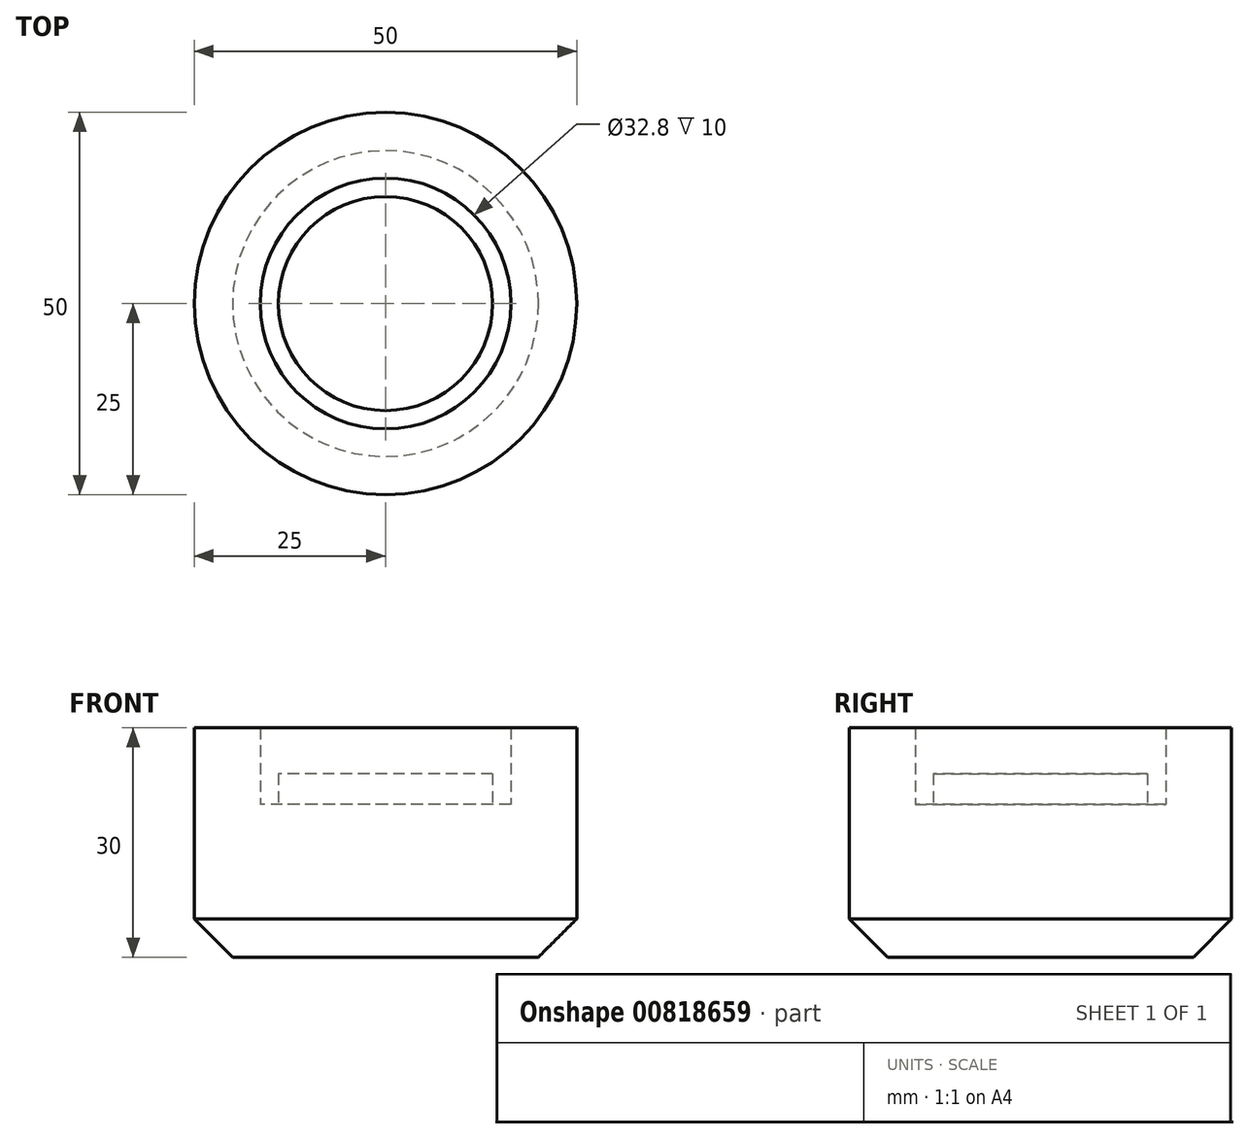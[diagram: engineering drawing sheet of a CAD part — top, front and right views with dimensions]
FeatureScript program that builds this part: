
annotation { "Feature Type Name" : "Feature", "Feature Type Description" : "" }
export const myFeature = defineFeature(function(context is Context, id is Id, definition is map)
    precondition{}
    {
        {
            var Q0;
            Q0=qCreatedBy(makeId("Top.planeOp"),FACE);
            var sketch = newSketch(context, id + "F0", { "sketchPlane" : qUnion([Q0])});
            skCircle(sketch, "E0", {"center": v(0, 0) * mm, "radius": 25 * mm});
            skSolve(sketch);
        }
        {
            var Q0;
            Q0=makeQuery(id+"F0.imprint","IMPRINT",FACE,{"disambiguationData":[TD([[makeQuery(id+"F0.imprint","IMPRINT",EDGE,{"derivedFrom":sQuery(id+"F0.wireOp",EDGE,"E0")}),1.0]])]});
            extrude(context, id + "F1", {"entities" : qUnion([Q0]), "depth" : 20 * mm, "offsetDistance" : 25 * mm});
        }
        {
            var Q0;
            Q0=makeQuery(id+"F1.opExtrude","CAP_FACE",FACE,{"disambiguationData":[OSD([sQuery(id+"F0.wireOp",EDGE,"E0")])],"isStart":false});
            var sketch = newSketch(context, id + "F2", { "sketchPlane" : qUnion([Q0])});
            skPoint(sketch, "E1.0", {"position": v(0, 0) * mm});
            skCircle(sketch, "E2", {"center": v(0, 0) * mm, "radius": 16.4 * mm});
            skCircle(sketch, "E3", {"center": v(0, 0) * mm, "radius": 14 * mm});
            skSolve(sketch);
        }
        {
            var Q0;
            Q0=makeQuery(id+"F2.imprint","IMPRINT",FACE,{"disambiguationData":[TD([[makeQuery(id+"F2.imprint","IMPRINT",EDGE,{"derivedFrom":sQuery(id+"F2.wireOp",EDGE,"E3")}),1.0]])]});
            extrude(context, id + "F3", {"entities" : qUnion([Q0]), "operationType" : NewBodyOperationType.ADD, "depth" : 4 * mm, "offsetDistance" : 25 * mm});
        }
        {
            var Q0;
            Q0=makeQuery(id+"F2.imprint","IMPRINT",FACE,{"disambiguationData":[TD([[makeQuery(id+"F2.imprint","IMPRINT",EDGE,{"derivedFrom":sQuery(id+"F2.wireOp",EDGE,"E2")}),-1.0]])]});
            extrude(context, id + "F4", {"entities" : qUnion([Q0]), "operationType" : NewBodyOperationType.ADD, "depth" : 10 * mm, "offsetDistance" : 25 * mm});
        }
        {
            var Q0;
            Q0=makeQuery(id+"F1.opExtrude","CAP_EDGE",EDGE,{"disambiguationData":[OSD([sQuery(id+"F0.wireOp",EDGE,"E0")])],"isStart":true});
            chamfer(context, id + "F5", {"entities" : qUnion([Q0]), "width" : 5 * mm, "tangentPropagation" : true});
        }
    });
